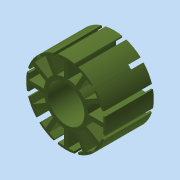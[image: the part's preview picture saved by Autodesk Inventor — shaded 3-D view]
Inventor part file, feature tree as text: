
AUTODESK INVENTOR PART (.ipt)
format: ipt  version: 2015 (Build 190159000, 159)  size: 202,240 bytes
history: native  units: in
note: dims shown in document units (in); Inventor stores cm internally (conversion verified against a paired STEP export)
features: extrude x1, pattern_circular x1, sketch x1
ambient origin geometry x8: Origin, YZ Plane, XZ Plane, XY Plane, X Axis, Y Axis, Z Axis, Center Point
bodies: Solid1 (feature_tree)
feature tree (3):
  extrude  "Extrusion1"  Depth=1.1811in
  pattern_circular  "Circular Pattern1"  [2 undecoded]
  sketch  "Sketch1"  dims[d0=0.9055in d1=1.9685in d2=0.1649in d3=1.1024in d4=4.7244in d6=360.0deg d8=1.1811in d9=0.0in d10=4.7244in d11=360.0deg]
note: 2 required parameter values undecoded (feature->parameter linkage not recoverable at this tier; creation-order binding heuristic only, values carry confidence <= 0.55)
